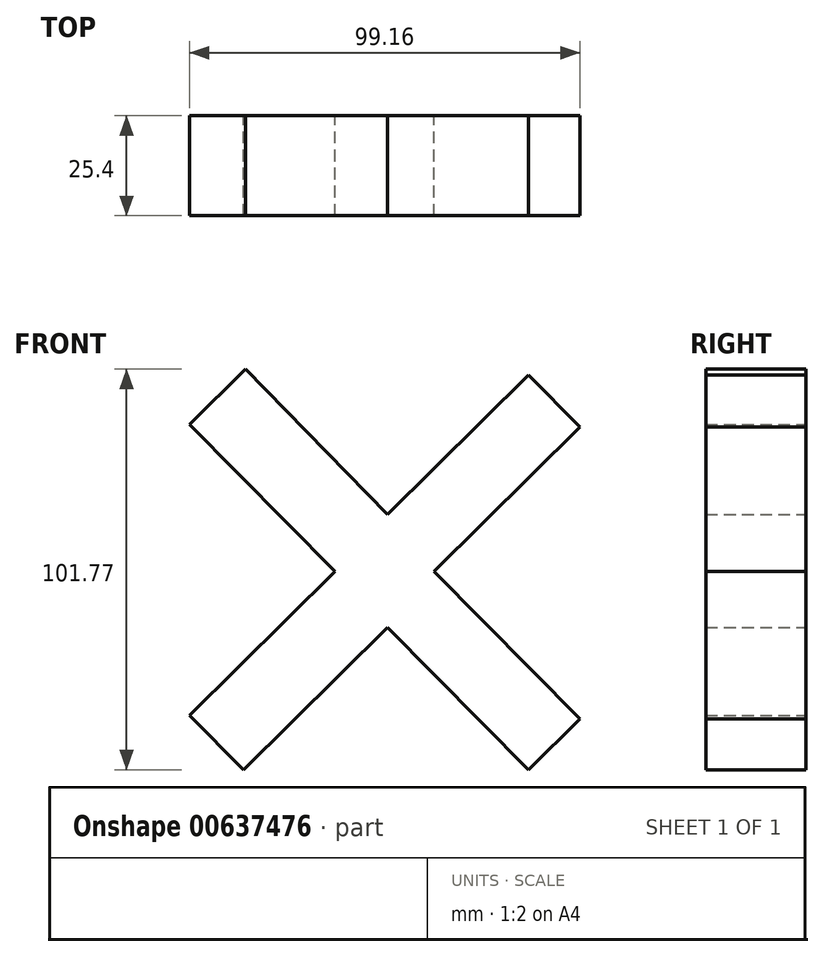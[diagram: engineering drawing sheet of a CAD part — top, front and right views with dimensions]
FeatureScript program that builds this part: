
annotation { "Feature Type Name" : "Feature", "Feature Type Description" : "" }
export const myFeature = defineFeature(function(context is Context, id is Id, definition is map)
    precondition{}
    {
        {
            var Q0;
            Q0=qCreatedBy(makeId("Front.planeOp"),FACE);
            var sketch = newSketch(context, id + "F0", { "sketchPlane" : qUnion([Q0])});
            skLineSegment(sketch, "E0", {"start": v(0, 14.41) * mm, "end": v(35.85, 49.89) * mm});
            skLineSegment(sketch, "E1", {"start": v(35.85, 49.89) * mm, "end": v(48.9, 36.7) * mm});
            skLineSegment(sketch, "E2", {"start": v(48.9, 36.7) * mm, "end": v(11.83, 0) * mm});
            skLineSegment(sketch, "E3", {"start": v(11.83, 0) * mm, "end": v(48.9, -37.46) * mm});
            skLineSegment(sketch, "E4", {"start": v(48.9, -37.46) * mm, "end": v(35.85, -50.39) * mm});
            skLineSegment(sketch, "E5", {"start": v(35.85, -50.39) * mm, "end": v(0, -14.17) * mm});
            skLineSegment(sketch, "E6", {"start": v(0, -14.17) * mm, "end": v(-36.6, -50.39) * mm});
            skLineSegment(sketch, "E7", {"start": v(-36.6, -50.39) * mm, "end": v(-50.26, -36.59) * mm});
            skLineSegment(sketch, "E8", {"start": v(-50.26, -36.59) * mm, "end": v(-13.29, 0) * mm});
            skLineSegment(sketch, "E9", {"start": v(-13.29, 0) * mm, "end": v(-50.26, 37.35) * mm});
            skLineSegment(sketch, "E10", {"start": v(-50.26, 37.35) * mm, "end": v(-36.08, 51.38) * mm});
            skLineSegment(sketch, "E11", {"start": v(-36.08, 51.38) * mm, "end": v(0, 14.41) * mm});
            skSolve(sketch);
        }
        {
            var Q0;
            Q0 = qSketchRegion(id + "F0", true);
            extrude(context, id + "F1", {"entities" : qUnion([Q0]), "endBound" : BoundingType.SYMMETRIC, "depth" : 25.4 * mm, "offsetDistance" : 25.4 * mm});
        }
    });
